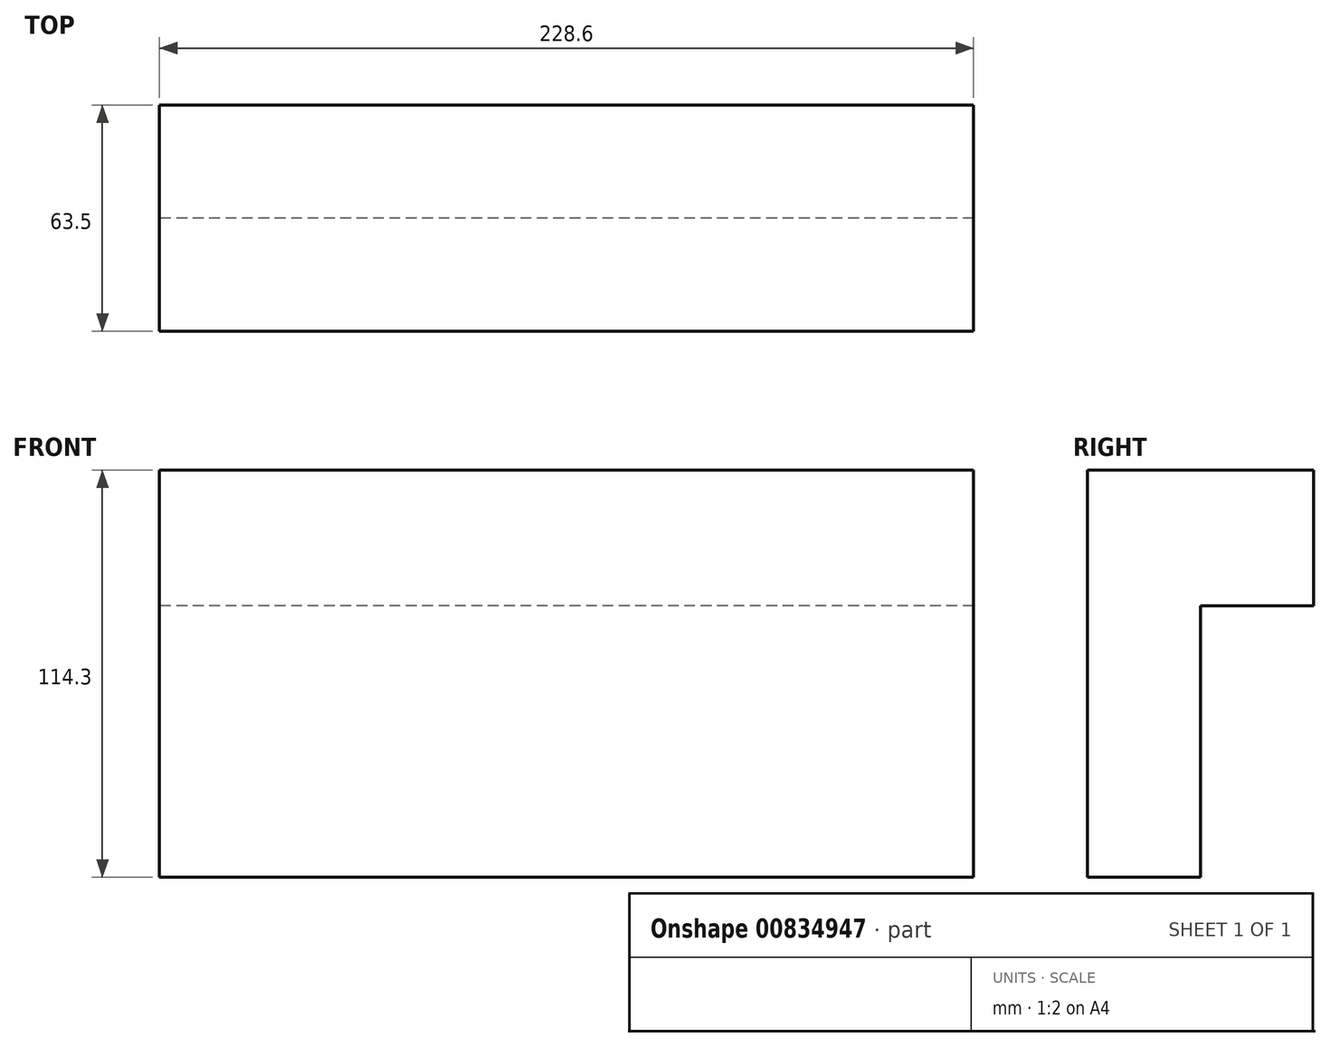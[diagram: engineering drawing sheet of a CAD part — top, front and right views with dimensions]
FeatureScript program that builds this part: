
annotation { "Feature Type Name" : "Feature", "Feature Type Description" : "" }
export const myFeature = defineFeature(function(context is Context, id is Id, definition is map)
    precondition{}
    {
        {
            var Q0;
            Q0=qCreatedBy(makeId("Right.planeOp"),FACE);
            var sketch = newSketch(context, id + "F0", { "sketchPlane" : qUnion([Q0])});
            skLineSegment(sketch, "E0.bottom", {"start": v(0, 0) * mm, "end": v(31.75, 0) * mm});
            skLineSegment(sketch, "E0.top", {"start": v(0, 114.3) * mm, "end": v(63.5, 114.3) * mm});
            skLineSegment(sketch, "E0.left", {"start": v(0, 0) * mm, "end": v(0, 114.3) * mm});
            skLineSegment(sketch, "E0.right", {"start": v(63.5, 76.2) * mm, "end": v(63.5, 114.3) * mm});
            skLineSegment(sketch, "E1.top", {"start": v(63.5, 76.2) * mm, "end": v(31.75, 76.2) * mm});
            skLineSegment(sketch, "E1.right", {"start": v(31.75, 0) * mm, "end": v(31.75, 76.2) * mm});
            skSolve(sketch);
        }
        {
            var Q0;
            Q0 = qSketchRegion(id + "F0", true);
            extrude(context, id + "F1", {"entities" : qUnion([Q0]), "depth" : 228.6 * mm, "offsetDistance" : 25.4 * mm});
        }
    });
